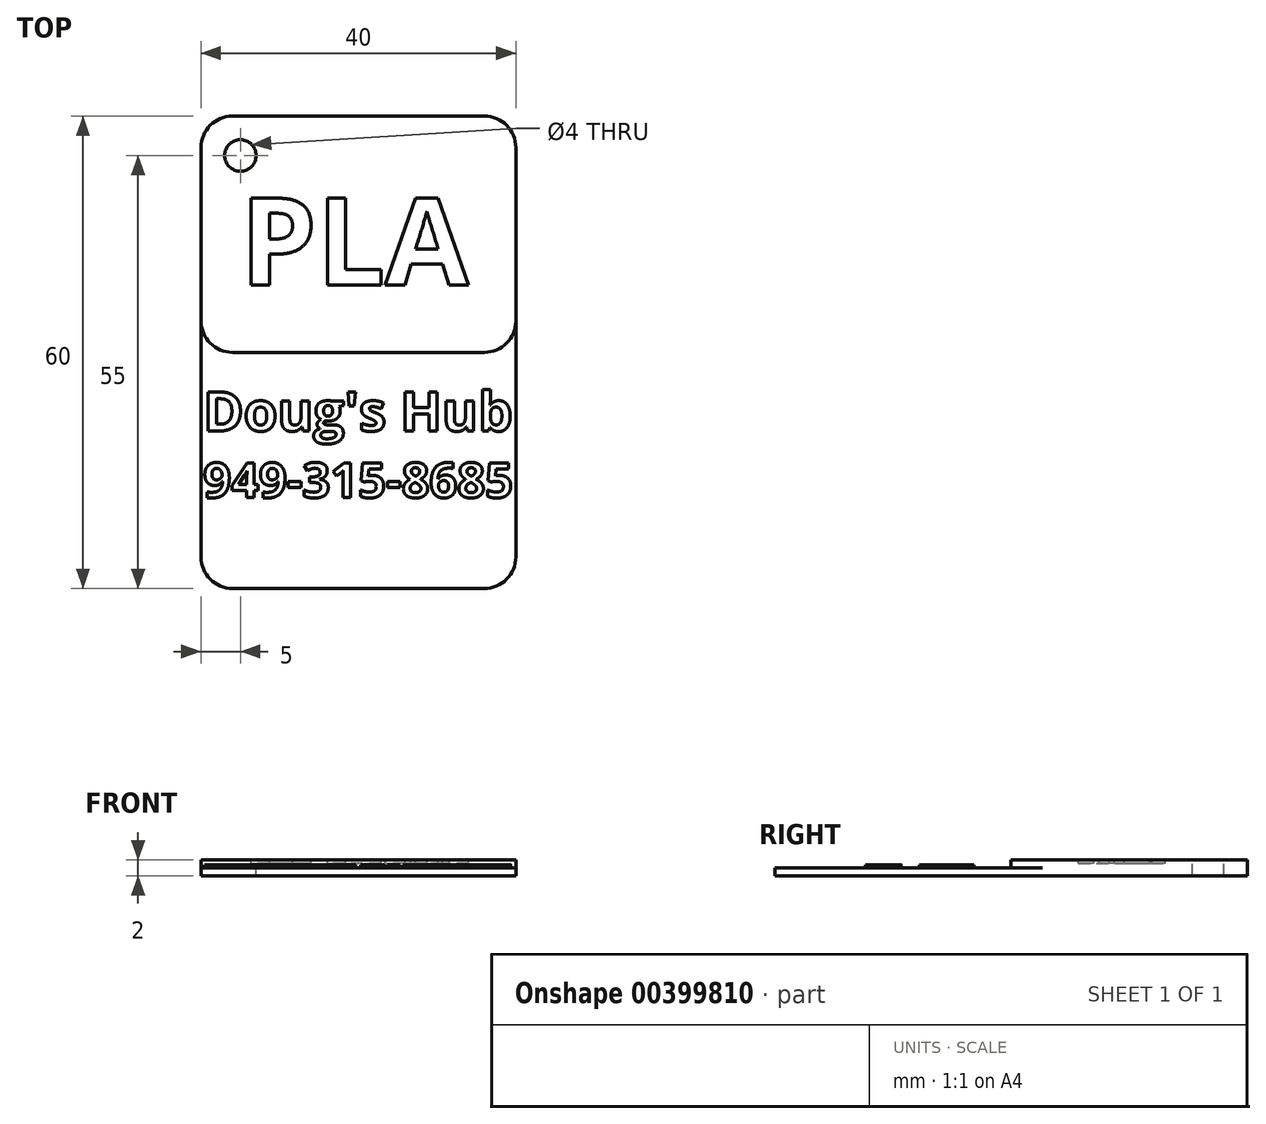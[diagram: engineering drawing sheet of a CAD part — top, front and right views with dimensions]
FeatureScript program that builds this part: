
annotation { "Feature Type Name" : "Feature", "Feature Type Description" : "" }
export const myFeature = defineFeature(function(context is Context, id is Id, definition is map)
    precondition{}
    {
        {
            var Q0;
            Q0=qCreatedBy(makeId("Top.planeOp"),FACE);
            var sketch = newSketch(context, id + "F0", { "sketchPlane" : qUnion([Q0])});
            skLineSegment(sketch, "E0.bottom", {"start": v(0, 0) * mm, "end": v(40, 0) * mm});
            skLineSegment(sketch, "E0.top", {"start": v(0, 60) * mm, "end": v(40, 60) * mm});
            skLineSegment(sketch, "E0.left", {"start": v(0, 0) * mm, "end": v(0, 60) * mm});
            skLineSegment(sketch, "E0.right", {"start": v(40, 0) * mm, "end": v(40, 60) * mm});
            skSolve(sketch);
        }
        {
            var Q0;
            Q0 = qSketchRegion(id + "F0", true);
            extrude(context, id + "F1", {"entities" : qUnion([Q0]), "depth" : 1 * mm});
        }
        {
            var Q0;
            Q0=makeQuery(id+"F1.opExtrude","CAP_FACE",FACE,{"disambiguationData":[OSD([sQuery(id+"F0.wireOp",EDGE,"E0.bottom"),sQuery(id+"F0.wireOp",EDGE,"E0.top"),sQuery(id+"F0.wireOp",EDGE,"E0.left"),sQuery(id+"F0.wireOp",EDGE,"E0.right")])],"isStart":false});
            var sketch = newSketch(context, id + "F2", { "sketchPlane" : qUnion([Q0])});
            skLineSegment(sketch, "E1.bottom", {"start": v(0, 60) * mm, "end": v(40, 60) * mm});
            skLineSegment(sketch, "E1.top", {"start": v(0, 30) * mm, "end": v(40, 30) * mm});
            skLineSegment(sketch, "E1.left", {"start": v(0, 60) * mm, "end": v(0, 30) * mm});
            skLineSegment(sketch, "E1.right", {"start": v(40, 60) * mm, "end": v(40, 30) * mm});
            skSolve(sketch);
        }
        {
            var Q0;
            Q0 = qSketchRegion(id + "F2", true);
            extrude(context, id + "F3", {"entities" : qUnion([Q0]), "operationType" : NewBodyOperationType.ADD, "depth" : 1 * mm});
        }
        {
            var Q0;
            Q0=makeQuery(id+"F1.opExtrude","CAP_FACE",FACE,{"disambiguationData":[OSD([sQuery(id+"F0.wireOp",EDGE,"E0.bottom"),sQuery(id+"F0.wireOp",EDGE,"E0.top"),sQuery(id+"F0.wireOp",EDGE,"E0.left"),sQuery(id+"F0.wireOp",EDGE,"E0.right")])],"isStart":false});
            var sketch = newSketch(context, id + "F4", { "sketchPlane" : qUnion([Q0])});
            skPoint(sketch, "E2.oppositeSnap0", {"position": v(20, 25) * mm});
            skLineSegment(sketch, "E2.bottom", {"start": v(24.97, 0) * mm, "end": v(24.97, 0) * mm});
            skText(sketch, "E3", { "text": "Doug\'s Hub", "fontName": "OpenSans-Bold.ttf"});
            skText(sketch, "E4", { "text": "949-315-8685", "fontName": "OpenSans-Bold.ttf"});
            const initialGuessF4  = {"E3": [0.00028, 0.02, 1, 0, 0.005], "E4": [0.00028, 0.01154, 1, 0, 0.00446]};
            skSetInitialGuess(sketch, initialGuessF4);
            skSolve(sketch);
        }
        {
            var Q0;
            Q0 = qSketchRegion(id + "F4", true);
            extrude(context, id + "F5", {"entities" : qUnion([Q0]), "operationType" : NewBodyOperationType.ADD, "depth" : .4 * mm});
        }
        {
            var Q0;
            Q0=makeQuery(id+"F3.opExtrude","CAP_FACE",FACE,{"disambiguationData":[OSD([sQuery(id+"F2.wireOp",EDGE,"E1.bottom"),sQuery(id+"F2.wireOp",EDGE,"E1.top"),sQuery(id+"F2.wireOp",EDGE,"E1.left"),sQuery(id+"F2.wireOp",EDGE,"E1.right")])],"isStart":false});
            var sketch = newSketch(context, id + "F6", { "sketchPlane" : qUnion([Q0])});
            skText(sketch, "E5", { "text": "PLA", "fontName": "OpenSans-Bold.ttf"});
            const initialGuessF6  = {"E5": [0.005, 0.03857, 1, 0, 0.01109]};
            skSetInitialGuess(sketch, initialGuessF6);
            skSolve(sketch);
        }
        {
            var Q0;
            Q0 = qSketchRegion(id + "F6", true);
            extrude(context, id + "F7", {"entities" : qUnion([Q0]), "operationType" : NewBodyOperationType.REMOVE, "oppositeDirection" : true, "depth" : .4 * mm});
        }
        {
            var Q0;
            {var subQ0=sQuery(id+"F2.wireOp",EDGE,"E1.left");var subQ1=sQuery(id+"F2.wireOp",EDGE,"E1.top");var subQ2=sQuery(id+"F2.wireOp",EDGE,"E1.bottom");var subQ3=sQuery(id+"F2.wireOp",EDGE,"E1.right");Q0=makeQuery(id+"F7.boolean.opBoolean","SPLIT",FACE,{"disambiguationData":[TD([makeQuery(id+"F1.opExtrude","SWEPT_FACE",FACE,{"disambiguationData":[OSD([sQuery(id+"F0.wireOp",EDGE,"E0.top")])]})])],"derivedFrom":makeQuery(id+"F3.opExtrude","CAP_FACE",FACE,{"disambiguationData":[OSD([subQ2,subQ1,subQ0,subQ3])],"isStart":false})});}
            var sketch = newSketch(context, id + "F8", { "sketchPlane" : qUnion([Q0])});
            skCircle(sketch, "E6", {"center": v(5, 55) * mm, "radius": 2 * mm});
            skSolve(sketch);
        }
        {
            var Q0;
            Q0 = qSketchRegion(id + "F8", true);
            extrude(context, id + "F9", {"entities" : qUnion([Q0]), "operationType" : NewBodyOperationType.REMOVE, "endBound" : BoundingType.THROUGH_ALL, "oppositeDirection" : true, "depth" : 25.4 * mm});
        }
        {
            var Q0;
            Q0=makeQuery(id+"F3.opExtrude","SWEPT_EDGE",EDGE,{"disambiguationData":[OSD([sQuery(id+"F0.wireOp",EDGE,"E0.left"),sQuery(id+"F2.wireOp",EDGE,"E1.top"),sQuery(id+"F2.wireOp",EDGE,"E1.left")])]});
            var Q1;
            Q1=makeQuery(id+"F3.opExtrude","SWEPT_EDGE",EDGE,{"disambiguationData":[OSD([sQuery(id+"F0.wireOp",EDGE,"E0.right"),sQuery(id+"F2.wireOp",EDGE,"E1.top"),sQuery(id+"F2.wireOp",EDGE,"E1.right")])]});
            var Q2;
            Q2=makeQuery(id+"F1.opExtrude","SWEPT_EDGE",EDGE,{"disambiguationData":[OSD([sQuery(id+"F0.wireOp",EDGE,"E0.bottom"),sQuery(id+"F0.wireOp",EDGE,"E0.left")])]});
            var Q3;
            Q3=makeQuery(id+"F1.opExtrude","SWEPT_EDGE",EDGE,{"disambiguationData":[OSD([sQuery(id+"F0.wireOp",EDGE,"E0.bottom"),sQuery(id+"F0.wireOp",EDGE,"E0.right")])]});
            var Q4;
            Q4=makeQuery(id+"F3.boolean.opBoolean","MERGE",EDGE,{"derivedFrom":[makeQuery(id+"F1.opExtrude","SWEPT_EDGE",EDGE,{"disambiguationData":[OSD([sQuery(id+"F0.wireOp",EDGE,"E0.top"),sQuery(id+"F0.wireOp",EDGE,"E0.right")])]}),makeQuery(id+"F3.opExtrude","SWEPT_EDGE",EDGE,{"disambiguationData":[OSD([sQuery(id+"F2.wireOp",EDGE,"E1.bottom"),sQuery(id+"F2.wireOp",EDGE,"E1.right")])]})]});
            var Q5;
            Q5=makeQuery(id+"F3.boolean.opBoolean","MERGE",EDGE,{"derivedFrom":[makeQuery(id+"F1.opExtrude","SWEPT_EDGE",EDGE,{"disambiguationData":[OSD([sQuery(id+"F0.wireOp",EDGE,"E0.top"),sQuery(id+"F0.wireOp",EDGE,"E0.left")])]}),makeQuery(id+"F3.opExtrude","SWEPT_EDGE",EDGE,{"disambiguationData":[OSD([sQuery(id+"F2.wireOp",EDGE,"E1.bottom"),sQuery(id+"F2.wireOp",EDGE,"E1.left")])]})]});
            fillet(context, id + "F10", {"entities" : qUnion([Q0, Q1, Q2, Q3, Q4, Q5]), "radius" : 4 * mm, "tangentPropagation" : true, "allowEdgeOverflow" : false});
        }
    });
